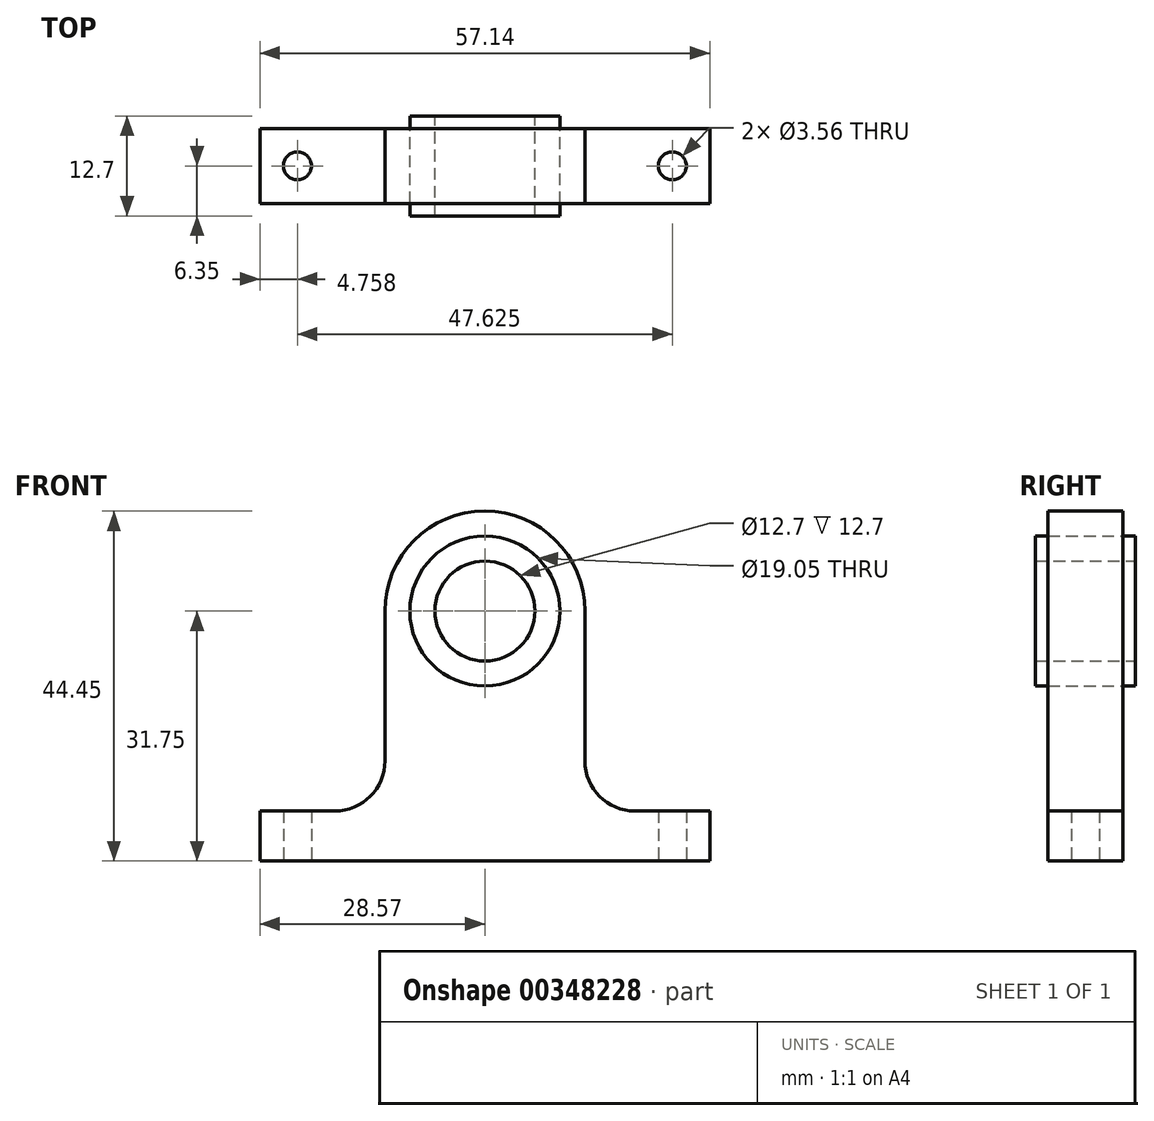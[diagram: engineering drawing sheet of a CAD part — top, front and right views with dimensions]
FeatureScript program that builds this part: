
annotation { "Feature Type Name" : "Feature", "Feature Type Description" : "" }
export const myFeature = defineFeature(function(context is Context, id is Id, definition is map)
    precondition{}
    {
        {
            var Q0;
            Q0=qCreatedBy(makeId("Front.planeOp"),FACE);
            var sketch = newSketch(context, id + "F0", { "sketchPlane" : qUnion([Q0])});
            skArc(sketch, "E0", {"start": v(-12.7, 0) * mm, "mid": v(0, 12.7) * mm, "end": v(12.7, 0) * mm});
            skLineSegment(sketch, "E1", {"start": v(-12.7, 0) * mm, "end": v(-12.7, -19.05) * mm});
            skLineSegment(sketch, "E2", {"start": v(-19.05, -25.4) * mm, "end": v(-28.58, -25.4) * mm});
            skLineSegment(sketch, "E3", {"start": v(-28.58, -25.4) * mm, "end": v(-28.58, -31.75) * mm});
            skLineSegment(sketch, "E4", {"start": v(-28.58, -31.75) * mm, "end": v(28.58, -31.75) * mm});
            skLineSegment(sketch, "E5", {"start": v(28.57, -31.75) * mm, "end": v(28.57, -25.4) * mm});
            skLineSegment(sketch, "E6", {"start": v(28.58, -25.4) * mm, "end": v(19.05, -25.4) * mm});
            skLineSegment(sketch, "E7", {"start": v(12.7, -19.05) * mm, "end": v(12.7, 0) * mm});
            skCircle(sketch, "E8", {"center": v(0, 0) * mm, "radius": 9.53 * mm});
            skPoint(sketch, "E9", {"position": v(0, -31.75) * mm});
            skPoint(sketch, "E10.visualSharp", {"position": v(-12.7, -25.4) * mm});
            skArc(sketch, "E10.filletArc", {"start": v(-19.05, -25.4) * mm, "mid": v(-14.56, -23.54) * mm, "end": v(-12.7, -19.05) * mm});
            skPoint(sketch, "E11.visualSharp", {"position": v(12.7, -25.4) * mm});
            skArc(sketch, "E11.filletArc", {"start": v(12.7, -19.05) * mm, "mid": v(14.56, -23.54) * mm, "end": v(19.05, -25.4) * mm});
            skSolve(sketch);
        }
        {
            var Q0;
            Q0=qSketchRegion(id+"F0",true);
            extrude(context, id + "F1", {"entities" : qUnion([Q0]), "endBound" : BoundingType.SYMMETRIC, "depth" : 9.52 * mm});
        }
        {
            var Q0;
            Q0=makeQuery(id+"F1.opExtrude","SWEPT_FACE",FACE,{"disambiguationData":[OSD([sQuery(id+"F0.wireOp",EDGE,"E4")])]});
            var sketch = newSketch(context, id + "F2", { "sketchPlane" : qUnion([Q0])});
            skPoint(sketch, "E12", {"position": v(23.81, 0) * mm});
            skPoint(sketch, "E13", {"position": v(-23.81, 0) * mm});
            skSolve(sketch);
        }
        {
            var Q0;
            Q0=sQuery(id+"F2.wireOp",VERTEX,"E13");
            var Q1;
            Q1=sQuery(id+"F2.wireOp",VERTEX,"E12");
            var Q2;
            Q2=makeQuery(id+"F1.opExtrude","SWEPT_BODY",BODY,{"disambiguationData":[OSD([sQuery(id+"F0.wireOp",EDGE,"E0"),sQuery(id+"F0.wireOp",EDGE,"E1"),sQuery(id+"F0.wireOp",EDGE,"E2"),sQuery(id+"F0.wireOp",EDGE,"E3"),sQuery(id+"F0.wireOp",EDGE,"E4"),sQuery(id+"F0.wireOp",EDGE,"E5"),sQuery(id+"F0.wireOp",EDGE,"E6"),sQuery(id+"F0.wireOp",EDGE,"E7"),sQuery(id+"F0.wireOp",EDGE,"E8"),sQuery(id+"F0.wireOp",EDGE,"E10.filletArc"),sQuery(id+"F0.wireOp",EDGE,"E11.filletArc")])]});
            hole(context, id + "F3", {"style" : HoleStyle.SIMPLE, "holeDiameter" : 3.56 * mm, "endStyle" : HoleEndStyle.THROUGH, "locations" : qUnion([Q0, Q1]), "scope" : qUnion([Q2])});
        }
        {
            var Q0;
            Q0=qCreatedBy(makeId("Front.planeOp"),FACE);
            var sketch = newSketch(context, id + "F4", { "sketchPlane" : qUnion([Q0])});
            skCircle(sketch, "E14", {"center": v(0, 0) * mm, "radius": 9.53 * mm});
            skCircle(sketch, "E15", {"center": v(0, 0) * mm, "radius": 6.35 * mm});
            skSolve(sketch);
        }
        {
            var Q0;
            Q0=qSketchRegion(id+"F4",true);
            extrude(context, id + "F5", {"entities" : qUnion([Q0]), "endBound" : BoundingType.SYMMETRIC, "depth" : 12.7 * mm});
        }
    });
